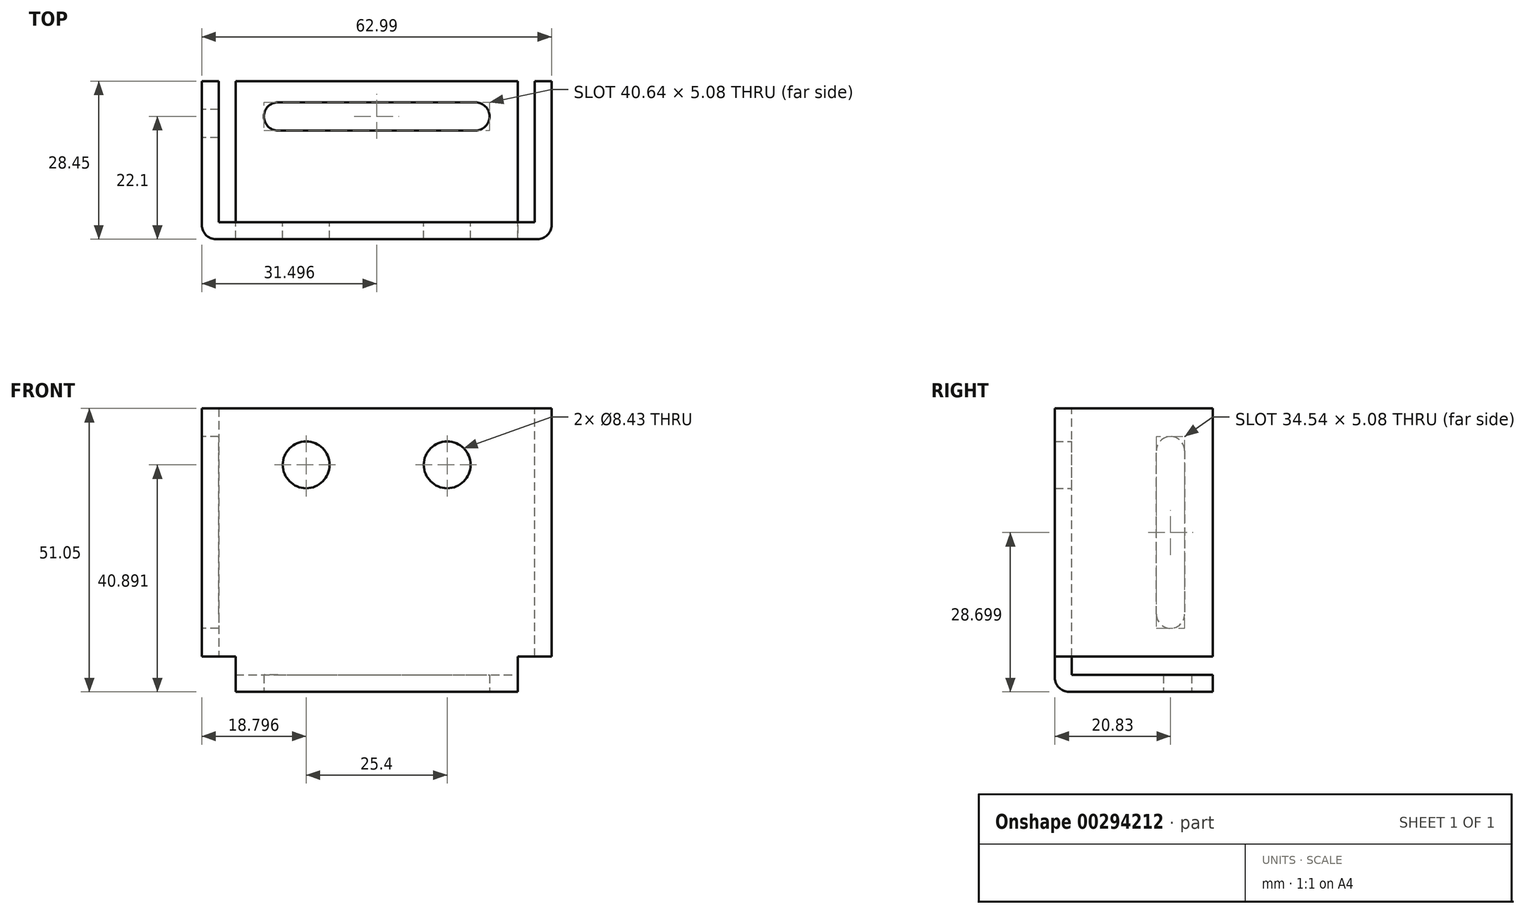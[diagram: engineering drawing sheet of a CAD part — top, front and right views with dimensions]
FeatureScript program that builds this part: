
annotation { "Feature Type Name" : "Feature", "Feature Type Description" : "" }
export const myFeature = defineFeature(function(context is Context, id is Id, definition is map)
    precondition{}
    {
        {
            var Q0;
            Q0=qCreatedBy(makeId("Front.planeOp"),FACE);
            var sketch = newSketch(context, id + "F0", { "sketchPlane" : qUnion([Q0])});
            skLineSegment(sketch, "E0", {"start": v(-33.12, 25.17) * mm, "end": v(-33.12, -19.53) * mm});
            skLineSegment(sketch, "E1", {"start": v(-33.12, -19.53) * mm, "end": v(-27.02, -19.53) * mm});
            skLineSegment(sketch, "E2", {"start": v(-27.02, -19.53) * mm, "end": v(-27.02, -25.88) * mm});
            skLineSegment(sketch, "E3", {"start": v(-27.02, -25.88) * mm, "end": v(23.78, -25.88) * mm});
            skLineSegment(sketch, "E4", {"start": v(23.78, -25.88) * mm, "end": v(23.78, -19.53) * mm});
            skLineSegment(sketch, "E5", {"start": v(23.78, -19.53) * mm, "end": v(29.87, -19.53) * mm});
            skLineSegment(sketch, "E6", {"start": v(29.87, -19.53) * mm, "end": v(29.87, 25.17) * mm});
            skLineSegment(sketch, "E7", {"start": v(29.87, 25.17) * mm, "end": v(-33.12, 25.17) * mm});
            skCircle(sketch, "E8", {"center": v(-14.32, 15.01) * mm, "radius": 4.22 * mm});
            skCircle(sketch, "E9", {"center": v(-14.32, 15.01) * mm, "radius": 2.25 * mm});
            skCircle(sketch, "E10", {"center": v(11.08, 15.01) * mm, "radius": 4.22 * mm});
            skCircle(sketch, "E11", {"center": v(11.08, 15.01) * mm, "radius": 2.25 * mm});
            skSolve(sketch);
        }
        {
            var Q0;
            Q0 = qSketchRegion(id + "F0", true);
            extrude(context, id + "F1", {"entities" : qUnion([Q0]), "depth" : 3.05 * mm});
        }
        {
            var Q0;
            Q0=makeQuery(id+"F1.opExtrude","SWEPT_FACE",FACE,{"disambiguationData":[OSD([sQuery(id+"F0.wireOp",EDGE,"E6")])]});
            var sketch = newSketch(context, id + "F2", { "sketchPlane" : qUnion([Q0])});
            skLineSegment(sketch, "E12", {"start": v(0, 25.17) * mm, "end": v(25.4, 25.17) * mm});
            skLineSegment(sketch, "E13", {"start": v(25.4, 25.17) * mm, "end": v(25.4, -19.53) * mm});
            skLineSegment(sketch, "E14", {"start": v(25.4, -19.53) * mm, "end": v(0, -19.53) * mm});
            skSolve(sketch);
        }
        {
            var Q0;
            Q0=makeQuery(id+"F1.opExtrude","SWEPT_FACE",FACE,{"disambiguationData":[OSD([sQuery(id+"F0.wireOp",EDGE,"E0")])]});
            var sketch = newSketch(context, id + "F3", { "sketchPlane" : qUnion([Q0])});
            skLineSegment(sketch, "E15", {"start": v(0, 25.17) * mm, "end": v(-25.4, 25.17) * mm});
            skLineSegment(sketch, "E16", {"start": v(-25.4, 25.17) * mm, "end": v(-25.4, -19.53) * mm});
            skLineSegment(sketch, "E17", {"start": v(-25.4, -19.53) * mm, "end": v(0, -19.53) * mm});
            skLineSegment(sketch, "E18", {"start": v(-20.32, 17.55) * mm, "end": v(-20.32, -11.91) * mm});
            skLineSegment(sketch, "E19", {"start": v(-15.24, -11.91) * mm, "end": v(-15.24, 17.55) * mm});
            skArc(sketch, "E20", {"start": v(-15.24, 17.55) * mm, "mid": v(-17.78, 20.1) * mm, "end": v(-20.32, 17.55) * mm});
            skArc(sketch, "E21", {"start": v(-20.32, -11.91) * mm, "mid": v(-17.78, -14.45) * mm, "end": v(-15.24, -11.91) * mm});
            skSolve(sketch);
        }
        {
            var Q0;
            Q0=makeQuery(id+"F1.opExtrude","SWEPT_FACE",FACE,{"disambiguationData":[OSD([sQuery(id+"F0.wireOp",EDGE,"E3")])]});
            var sketch = newSketch(context, id + "F4", { "sketchPlane" : qUnion([Q0])});
            skLineSegment(sketch, "E22", {"start": v(-27.02, 0) * mm, "end": v(-27.02, -25.4) * mm});
            skLineSegment(sketch, "E23", {"start": v(-27.02, -25.4) * mm, "end": v(23.78, -25.4) * mm});
            skLineSegment(sketch, "E24", {"start": v(23.78, -25.4) * mm, "end": v(23.78, 0) * mm});
            skLineSegment(sketch, "E25", {"start": v(-19.4, -16.51) * mm, "end": v(16.16, -16.51) * mm});
            skLineSegment(sketch, "E26", {"start": v(-19.4, -21.6) * mm, "end": v(16.16, -21.59) * mm});
            skLineSegment(sketch, "E27", {"start": v(-19.4, -16.51) * mm, "end": v(-19.4, -21.6) * mm});
            skLineSegment(sketch, "E28", {"start": v(16.16, -16.51) * mm, "end": v(16.16, -21.6) * mm});
            skArc(sketch, "E29", {"start": v(-19.4, -16.51) * mm, "mid": v(-21.94, -19.05) * mm, "end": v(-19.4, -21.6) * mm});
            skArc(sketch, "E30", {"start": v(16.16, -21.59) * mm, "mid": v(18.7, -19.05) * mm, "end": v(16.16, -16.51) * mm});
            skSolve(sketch);
        }
        {
            var Q0;
            Q0=makeQuery(id+"F3.imprint","IMPRINT",FACE,{"disambiguationData":[TD([[makeQuery(id+"F3.imprint","IMPRINT",EDGE,{"derivedFrom":sQuery(id+"F3.wireOp",EDGE,"E15")}),1.0]])]});
            extrude(context, id + "F5", {"entities" : qUnion([Q0]), "operationType" : NewBodyOperationType.ADD, "oppositeDirection" : true, "depth" : 3.05 * mm});
        }
        {
            var Q0;
            Q0=makeQuery(id+"F4.imprint","IMPRINT",FACE,{"disambiguationData":[TD([[makeQuery(id+"F4.imprint","IMPRINT",EDGE,{"derivedFrom":sQuery(id+"F4.wireOp",EDGE,"E22")}),1.0]])]});
            extrude(context, id + "F6", {"entities" : qUnion([Q0]), "operationType" : NewBodyOperationType.ADD, "oppositeDirection" : true, "depth" : 3.05 * mm});
        }
        {
            var Q0;
            Q0=makeQuery(id+"F2.imprint","IMPRINT",FACE,{"disambiguationData":[TD([[makeQuery(id+"F2.imprint","IMPRINT",EDGE,{"derivedFrom":sQuery(id+"F2.wireOp",EDGE,"E12")}),-1.0]])]});
            extrude(context, id + "F7", {"entities" : qUnion([Q0]), "operationType" : NewBodyOperationType.ADD, "oppositeDirection" : true, "depth" : 3.05 * mm});
        }
        {
            var Q0;
            Q0=makeQuery(id+"F1.opExtrude","CAP_EDGE",EDGE,{"disambiguationData":[OSD([sQuery(id+"F0.wireOp",EDGE,"E0")])],"isStart":false});
            var Q1;
            Q1=makeQuery(id+"F5.opExtrude","CAP_EDGE",EDGE,{"disambiguationData":[OSD([sQuery(id+"F0.wireOp",EDGE,"E0")])],"isStart":false});
            var Q2;
            Q2=makeQuery(id+"F1.opExtrude","CAP_EDGE",EDGE,{"disambiguationData":[OSD([sQuery(id+"F0.wireOp",EDGE,"E6")])],"isStart":false});
            var Q3;
            Q3=makeQuery(id+"F7.opExtrude","CAP_EDGE",EDGE,{"disambiguationData":[OSD([sQuery(id+"F0.wireOp",EDGE,"E6")])],"isStart":false});
            var Q4;
            Q4=makeQuery(id+"F6.opExtrude","CAP_EDGE",EDGE,{"disambiguationData":[OSD([sQuery(id+"F0.wireOp",EDGE,"E3")])],"isStart":false});
            var Q5;
            Q5=makeQuery(id+"F1.opExtrude","CAP_EDGE",EDGE,{"disambiguationData":[OSD([sQuery(id+"F0.wireOp",EDGE,"E3")])],"isStart":false});
            fillet(context, id + "F8", {"entities" : qUnion([Q0, Q1, Q2, Q3, Q4, Q5]), "radius" : 2.54 * mm, "tangentPropagation" : true, "allowEdgeOverflow" : false});
        }
    });
